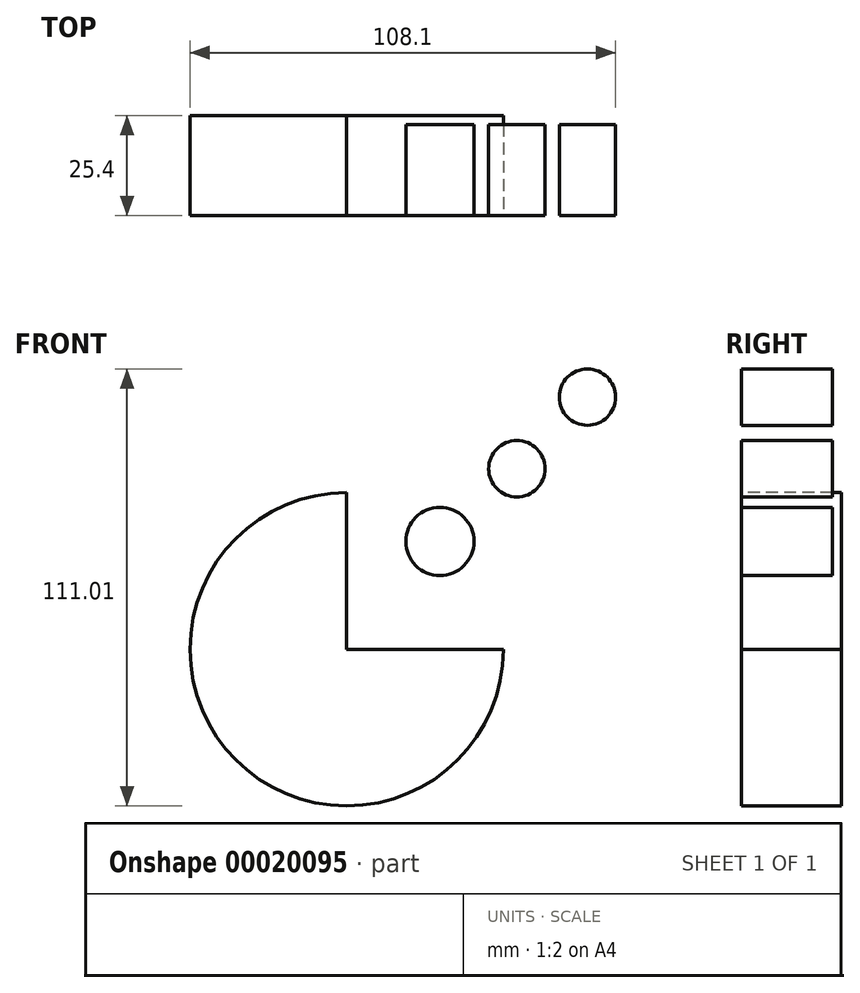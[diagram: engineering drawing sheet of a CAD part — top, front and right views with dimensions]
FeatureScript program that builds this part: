
annotation { "Feature Type Name" : "Feature", "Feature Type Description" : "" }
export const myFeature = defineFeature(function(context is Context, id is Id, definition is map)
    precondition{}
    {
        {
            var Q0;
            Q0=qCreatedBy(makeId("Front.planeOp"),FACE);
            var sketch = newSketch(context, id + "F0", { "sketchPlane" : qUnion([Q0])});
            skArc(sketch, "E0", {"start": v(0, 39.8) * mm, "mid": v(-28.15, -28.15) * mm, "end": v(39.8, 0) * mm});
            skLineSegment(sketch, "E1", {"start": v(0, 39.8) * mm, "end": v(0, 0) * mm});
            skLineSegment(sketch, "E2", {"start": v(39.8, 0) * mm, "end": v(0, 0) * mm});
            skSolve(sketch);
        }
        {
            var Q0;
            Q0=qCreatedBy(makeId("Front.planeOp"),FACE);
            var sketch = newSketch(context, id + "F1", { "sketchPlane" : qUnion([Q0])});
            skCircle(sketch, "E3", {"center": v(23.67, 27.4) * mm, "radius": 8.66 * mm});
            skCircle(sketch, "E4", {"center": v(43.23, 45.86) * mm, "radius": 7.17 * mm});
            skCircle(sketch, "E5", {"center": v(61.15, 64.06) * mm, "radius": 7.14 * mm});
            skSolve(sketch);
        }
        {
            var Q0;
            Q0=makeQuery(id+"F0.imprint","IMPRINT",FACE,{"disambiguationData":[TD([[makeQuery(id+"F0.imprint","IMPRINT",EDGE,{"derivedFrom":sQuery(id+"F0.wireOp",EDGE,"E0")}),1.0]])]});
            extrude(context, id + "F2", {"entities" : qUnion([Q0]), "oppositeDirection" : true, "depth" : 25.4 * mm});
        }
        {
            var Q0;
            Q0=makeQuery(id+"F1.imprint","IMPRINT",FACE,{"disambiguationData":[TD([[makeQuery(id+"F1.imprint","IMPRINT",EDGE,{"derivedFrom":sQuery(id+"F1.wireOp",EDGE,"E3")}),1.0]])]});
            var Q1;
            Q1=makeQuery(id+"F1.imprint","IMPRINT",FACE,{"disambiguationData":[TD([[makeQuery(id+"F1.imprint","IMPRINT",EDGE,{"derivedFrom":sQuery(id+"F1.wireOp",EDGE,"E4")}),1.0]])]});
            var Q2;
            Q2=makeQuery(id+"F1.imprint","IMPRINT",FACE,{"disambiguationData":[TD([[makeQuery(id+"F1.imprint","IMPRINT",EDGE,{"derivedFrom":sQuery(id+"F1.wireOp",EDGE,"E5")}),1.0]])]});
            extrude(context, id + "F3", {"entities" : qUnion([Q0, Q1, Q2]), "oppositeDirection" : true, "depth" : 23.08 * mm});
        }
    });
